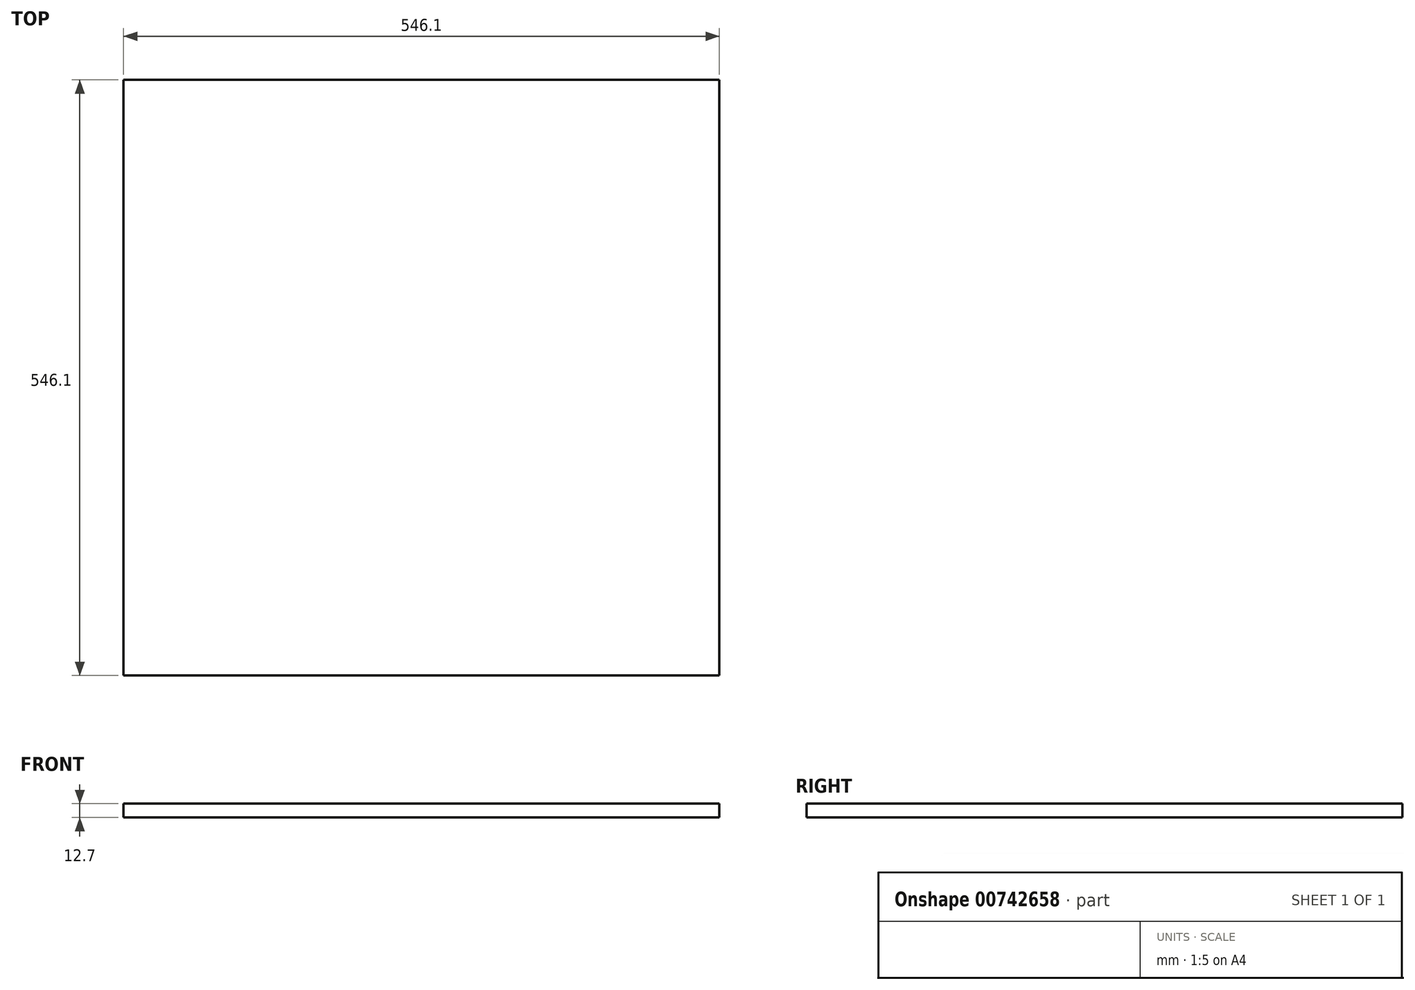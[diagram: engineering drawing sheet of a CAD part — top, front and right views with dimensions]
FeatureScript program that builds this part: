
annotation { "Feature Type Name" : "Feature", "Feature Type Description" : "" }
export const myFeature = defineFeature(function(context is Context, id is Id, definition is map)
    precondition{}
    {
        {
            var Q0;
            Q0=qCreatedBy(makeId("Top.planeOp"),FACE);
            var sketch = newSketch(context, id + "F0", { "sketchPlane" : qUnion([Q0])});
            skLineSegment(sketch, "E0.bottom", {"start": v(-273.05, 273.05) * mm, "end": v(273.05, 273.05) * mm});
            skLineSegment(sketch, "E0.top", {"start": v(-273.05, -273.05) * mm, "end": v(273.05, -273.05) * mm});
            skLineSegment(sketch, "E0.left", {"start": v(-273.05, 273.05) * mm, "end": v(-273.05, -273.05) * mm});
            skLineSegment(sketch, "E0.right", {"start": v(273.05, 273.05) * mm, "end": v(273.05, -273.05) * mm});
            skPoint(sketch, "E0.middle", {"position": v(0, 0) * mm});
            skSolve(sketch);
        }
        {
            var Q0;
            Q0=makeQuery(id+"F0.imprint","IMPRINT",FACE,{"disambiguationData":[TD([[makeQuery(id+"F0.imprint","IMPRINT",EDGE,{"derivedFrom":sQuery(id+"F0.wireOp",EDGE,"E0.bottom")}),-1.0]])]});
            extrude(context, id + "F1", {"entities" : qUnion([Q0]), "depth" : 12.7 * mm, "offsetDistance" : 25.4 * mm});
        }
    });
